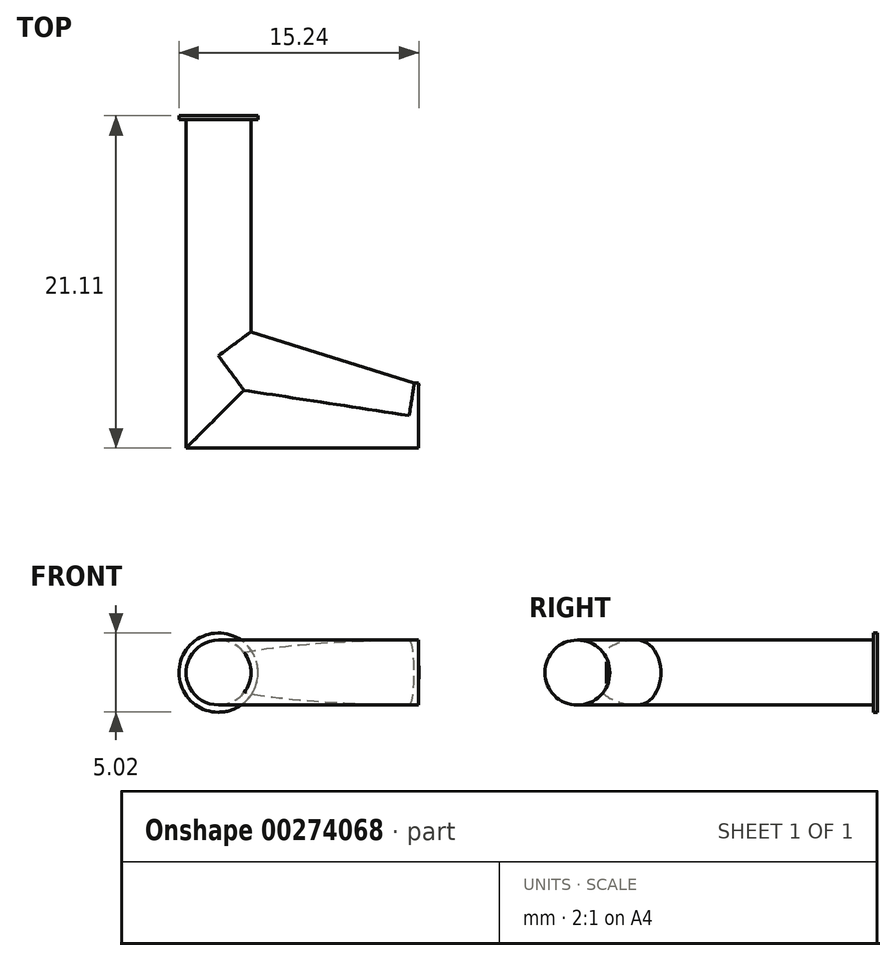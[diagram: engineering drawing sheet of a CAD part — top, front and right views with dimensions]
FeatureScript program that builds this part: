
annotation { "Feature Type Name" : "Feature", "Feature Type Description" : "" }
export const myFeature = defineFeature(function(context is Context, id is Id, definition is map)
    precondition{}
    {
        {
            var Q0;
            Q0=qCreatedBy(makeId("Front.planeOp"),FACE);
            var sketch = newSketch(context, id + "F0", { "sketchPlane" : qUnion([Q0])});
            skCircle(sketch, "E0", {"center": v(0, 0) * mm, "radius": 2.06 * mm});
            skSolve(sketch);
        }
        {
            var Q0;
            Q0=makeQuery(id+"F0.imprint","IMPRINT",FACE,{"disambiguationData":[TD([[makeQuery(id+"F0.imprint","IMPRINT",EDGE,{"derivedFrom":sQuery(id+"F0.wireOp",EDGE,"E0")}),1.0]])]});
            extrude(context, id + "F1", {"entities" : qUnion([Q0]), "depth" : 12.7 * mm});
        }
        {
            var Q0;
            Q0=qCreatedBy(makeId("Top.planeOp"),FACE);
            var sketch = newSketch(context, id + "F2", { "sketchPlane" : qUnion([Q0])});
            skLineSegment(sketch, "E1", {"start": v(0, 0) * mm, "end": v(0, -19.05) * mm});
            skLineSegment(sketch, "E2", {"start": v(0, -19.05) * mm, "end": v(12.7, -19.05) * mm});
            skLineSegment(sketch, "E3", {"start": v(0, 0) * mm, "end": v(0, -15.24) * mm});
            skLineSegment(sketch, "E4", {"start": v(0, -15.24) * mm, "end": v(12.12, -19.05) * mm});
            skSolve(sketch);
        }
        {
            var Q0;
            Q0=makeQuery(id+"F1.opExtrude","CAP_FACE",FACE,{"disambiguationData":[OSD([sQuery(id+"F0.wireOp",EDGE,"E0")])],"isStart":true});
            var Q1;
            Q1=sQuery(id+"F2.wireOp",EDGE,"E1");
            var Q2;
            Q2=sQuery(id+"F2.wireOp",EDGE,"E2");
            sweep(context, id + "F3", {"operationType" : NewBodyOperationType.ADD, "profiles" : qUnion([Q0]), "path" : qUnion([Q1, Q2])});
        }
        {
            var Q0;
            Q0=makeQuery(id+"F1.opExtrude","CAP_FACE",FACE,{"disambiguationData":[OSD([sQuery(id+"F0.wireOp",EDGE,"E0")])],"isStart":true});
            var Q1;
            Q1=sQuery(id+"F2.wireOp",EDGE,"E3");
            var Q2;
            Q2=sQuery(id+"F2.wireOp",EDGE,"E4");
            sweep(context, id + "F4", {"operationType" : NewBodyOperationType.ADD, "profiles" : qUnion([Q0]), "path" : qUnion([Q1, Q2])});
        }
        {
            var Q0;
            Q0=qCreatedBy(makeId("Front.planeOp"),FACE);
            var sketch = newSketch(context, id + "F5", { "sketchPlane" : qUnion([Q0])});
            skCircle(sketch, "E5", {"center": v(0, 0) * mm, "radius": 2.51 * mm});
            skSolve(sketch);
        }
        {
            var Q0;
            Q0=makeQuery(id+"F5.imprint","IMPRINT",FACE,{"disambiguationData":[TD([[makeQuery(id+"F5.imprint","IMPRINT",EDGE,{"derivedFrom":sQuery(id+"F5.wireOp",EDGE,"E5")}),1.0]])]});
            extrude(context, id + "F6", {"entities" : qUnion([Q0]), "operationType" : NewBodyOperationType.ADD, "depth" : 0.25 * mm});
        }
    });
